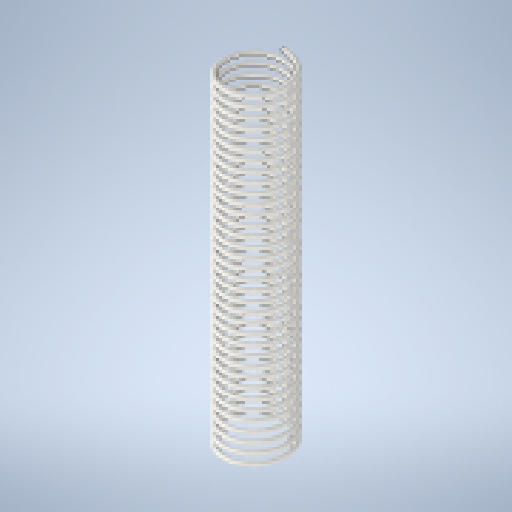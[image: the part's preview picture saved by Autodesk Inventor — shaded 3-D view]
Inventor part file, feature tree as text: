
AUTODESK INVENTOR PART (.ipt)
format: ipt  version: 2025 (Build 290162010, 162A)  size: 1,868,800 bytes
history: native  units: mm
features: sketch x97, plane x32, other x32, sweep x22, extrude x10, helix x4
ambient origin geometry x8: Origin, YZ Plane, XZ Plane, XY Plane, X Axis, Y Axis, Z Axis, Center Point
bodies: Solid1 (feature_tree)
feature tree (197):
  sketch  "3D Sketch2"
  plane  "ArbeitsebeneSweeping1"
  sweep  "Sweep1"
  other  "Erste Umdrehung mit Ösentyp 0(Rechts)"
  sketch  "Sketch8"  dims[d5=0.0mm d6=90.0deg d7=90.0deg d8=0.0mm d9=0.0mm d12=0.2mm]
  plane  "ArbeitsebeneExtrusion7"
  sketch  "Sketch10"  dims[d17=90.0deg d24=0.0mm d25=0.39411mm]
  plane  "ArbeitsebeneSweeping2"
  sweep  "Sweep2"
  other  "Zweite Umdrehung mit Ösentyp 0(Rechts)"
  sketch  "Sketch12"  dims[d26=10.0mm d27=347.619048mm]
  plane  "ArbeitsebeneExtrusion8"
  sketch  "Sketch110"  dims[d396=50.0mm]
  sketch  "3D Sketch20"
  plane  "ArbeitsebeneSweeping3"
  sweep  "Sweep3"
  sketch  "3D Sketch3"
  plane  "ArbeitsebeneSweeping6"
  sweep  "Sweep6"
  other  "Erste Umdrehung mit Ösentyp 0(Links)"
  sketch  "Sketch24"  dims[d171=0.0mm d172=90.0deg]
  plane  "ArbeitsebeneExtrusion5"
  sketch  "Sketch18"  dims[d86=90.0deg d87=20.0mm d90=20.0mm]
  plane  "ArbeitsebeneSweeping7"
  sweep  "Sweep7"
  other  "Zweite Umdrehung mit Ösentyp 0(Links)"
  sketch  "Sketch20"  dims[d149=90.0deg d152=20.0mm]
  plane  "ArbeitsebeneExtrusion6"
  sketch  "Sketch22"  dims[d169=300.0deg d170=1.075mm]
  plane  "ArbeitsebeneSweeping8"
  sweep  "Sweep8"
  other  "Erste Umdrehung mit Ösentyp 1(Links)"
  sketch  "Sketch27"  dims[d175=0.0mm d176=300.0deg]
  plane  "ArbeitsebeneExtrusion9"
  extrude  "Extrusion9"  Depth=10.0mm
  sketch  "Sketch29"  dims[d179=30.0mm d180=90.0deg]
  plane  "ArbeitsebeneSweeping9"
  sweep  "Sweep9"
  other  "Zweite Umdrehung mit Ösentyp 1(Links)"
  sketch  "Sketch32"  dims[d183=0.0mm d184=30.0mm d185=30.0mm d186=30.0mm]
  plane  "ArbeitsebeneExtrusion10"
  sketch  "Sketch34"  dims[d189=1.25mm d190=0.0mm]
  sketch  "3D Sketch22"
  plane  "ArbeitsebeneSweeping10"
  sweep  "Sweep10"
  other  "Erste Umdrehung mit Ösentyp 1(Rechts)"
  sketch  "Sketch42"  dims[d195=40.0mm d196=1.25mm]
  plane  "ArbeitsebeneExtrusion11"
  extrude  "Extrusion11"  Depth=20.0mm
  sketch  "Sketch44"  dims[d199=300.0deg d200=1.075mm]
  plane  "ArbeitsebeneSweeping11"
  sweep  "Sweep11"
  other  "Zweite Umdrehung mit Ösentyp 1(Rechts)"
  sketch  "Sketch112"  dims[d397=29.670597mm]
  plane  "ArbeitsebeneExtrusion12"
  sketch  "Sketch114"  dims[d401=50.0mm]
  sketch  "3D Sketch24"
  plane  "ArbeitsebeneSweeping12"
  sweep  "Sweep12"
  sketch  "Sketch46"  dims[d201=0.0mm d202=90.0deg]
  other  "Erstes Sweeping mit Ösentyp 2(Links)"
  sweep  "SweepingLinksÖse21"
  sketch  "Sketch48"  dims[d206=300.0deg d207=1.075mm]
  other  "Zweites Sweeping mit Ösentyp 2(Links)"
  sweep  "SweepingLinksÖse22"
  sketch  "Sketch50"  dims[d210=1.25mm d211=0.0mm d212=90.0deg d213=300.0deg d214=1.075mm]
  other  "Erstes Sweeping mit Ösentyp 2(Rechts)"
  sweep  "SweepingRechtsÖse21"
  sketch  "Sketch52"  dims[d220=50.0mm]
  other  "Zweites Sweeping mit Ösentyp 2(Rechts)"
  sweep  "SweepingRechtsÖse22"
  other  "Erste Umdrehung mit Ösentyp 3(Links)"
  extrude  "Extrusion1"  TaperAngle=90.0deg  [1 undecoded]
  sweep  "Sweep19"
  other  "Zweite Umdrehung mit Ösentyp 3(Links)"
  extrude  "Extrusion2"  Depth=30.0mm
  sketch  "Sketch60"  dims[d242=90.0deg]
  plane  "ArbeitsebeneSweeping20"
  sweep  "Sweep20"
  other  "Erste Umdrehung mit Ösentyp 3(Rechts)"
  extrude  "Extrusion3"  TaperAngle=0.0deg  [1 undecoded]
  sweep  "Sweep21"
  other  "Zweite Umdrehung mit Ösentyp 3(Rechts)"
  extrude  "Extrusion4"  TaperAngle=90.0deg  [1 undecoded]
  sketch  "Sketch68"  dims[d282=60.0mm]
  plane  "Work Plane46"
  sweep  "Sweep22"
  other  "Erste Umdrehung mit Ösentyp 4(Links)"
  sketch  "Sketch71"  dims[d301=10.0mm d302=15.0mm d303=0.0mm d304=90.0deg d305=90.0deg d306=0.0mm d307=0.0mm]
  plane  "ArbeitsebeneExtrusion13"
  extrude  "Extrusion13"  TaperAngle=90.0deg  [1 undecoded]
  sketch  "Sketch73"  dims[d310=0.7mm]
  plane  "ArbeitsebeneSweeping23"
  sweep  "Sweep23"
  other  "Zweite Umdrehung mit Ösentyp 4(Links)"
  sketch  "Sketch76"  dims[d320=1.125mm]
  plane  "ArbeitsebeneExtrusion14"
  sketch  "Sketch78"  dims[d322=10.0mm d323=15.0mm d324=0.0mm d325=90.0deg d326=90.0deg d327=0.0mm d328=0.0mm d329=70.0mm]
  sketch  "3D Sketch26"
  plane  "ArbeitsebeneSweeping24"
  sweep  "Sweep24"
  other  "Erste Umdrehung mit Ösentyp 4(Rechts)"
  sketch  "Sketch86"  dims[d332=10.0mm d333=15.0mm d334=0.0mm d335=90.0deg d336=90.0deg d337=0.0mm d338=0.0mm d339=70.0mm]
  plane  "Work PlaneExtrusion15"
  extrude  "Extrusion15"  Depth=1.25mm TaperAngle=0.0deg
  sketch  "Sketch88"  dims[d361=10.0mm]
  plane  "ArbeitsebeneSweeping25"
  sweep  "Sweep25"
  other  "Zweite Umdrehung mit Ösentyp 4(Rechts)"
  sketch  "Sketch116"  dims[d404=1.0mm]
  plane  "ArbeitsebeneExtrusion16"
  sketch  "Sketch118"  dims[d406=50.0mm d407=29.670597mm d408=0.0mm d411=60.0mm d423=60.0mm d433=1.0mm d434=0.0mm d435=1.075mm d436=0.7mm d437=10.0mm d438=15.0mm d439=0.0mm d440=90.0deg d441=90.0deg d442=0.0mm d443=0.0mm d444=60.0mm d447=60.0mm d457=1.0mm d458=0.0mm d459=60.0mm d469=90.0deg d478=90.0deg d479=1.075mm d480=0.7mm d481=25.4mm d482=15.0mm d483=0.0mm d484=90.0deg d485=90.0deg d486=0.0mm d487=0.0mm d491=10.0mm d498=10.0mm d501=0.0mm d502=1.0mm d503=0.0mm d504=210.0deg d505=0.0mm d506=0.0mm d507=1.0mm d508=0.0mm d509=29.670597mm d510=0.0mm d511=10.0mm d512=0.0mm d513=1.0mm d514=0.0mm d515=29.670597mm d516=0.0mm d517=0.0mm d518=1.0mm d519=0.0mm d520=1.075mm d521=0.7mm d522=10.0mm d523=15.0mm d524=0.0mm d525=90.0deg d526=90.0deg d527=0.0mm d528=0.0mm d529=60.0mm d530=50.0mm d531=0.0mm d532=1.0mm d533=0.0mm d534=20.0mm d535=210.0deg d536=0.0mm d537=0.0mm d538=1.0mm d539=0.0mm d540=29.670597mm d541=0.0mm d542=50.0mm d543=0.0mm d544=1.0mm d545=0.0mm d546=60.0mm d547=1.075mm d548=0.7mm d549=10.0mm d550=15.0mm d551=0.0mm d552=90.0deg d553=90.0deg d554=0.0mm d555=0.0mm d561=10.0mm d564=0.0mm d565=1.0mm d566=0.0mm d567=10.0mm d569=29.670597mm d570=0.0mm d571=90.0deg d578=0.0mm d579=0.2mm d580=1.0mm d581=0.0mm d584=10.0mm d585=10.0mm d588=29.670597mm d589=0.0mm d590=0.0mm d591=0.0mm d592=0.0mm d593=0.0mm d594=0.0mm d595=0.0mm d596=0.0mm d597=0.0mm d598=0.0mm d599=0.0mm d600=0.0mm d601=0.0mm d602=0.0mm d603=0.0mm d604=0.0mm d605=0.0mm d606=0.0mm d607=0.0mm d608=0.0mm d609=0.0mm d610=0.0mm d611=0.0mm]
  sketch  "3D Sketch28"
  plane  "ArbeitsebeneSweeping26"
  sweep  "Sweep26"
  other  "Erste Umdrehung mit Ösentyp 5(Links)"
  sketch  "Sketch91"  dims[d365=0.0mm]
  plane  "ArbeitsebeneExtrusion17"
  extrude  "Extrusion17"  TaperAngle=0.0deg  [1 undecoded]
  helix  "Coil1"  [1 undecoded]
  other  "Zweite Umdrehung mit Ösentyp 5(Links)"
  sketch  "Sketch95"  dims[d373=20.0mm]
  plane  "ArbeitsebeneExtrusion18"
  helix  "Coil2"  [1 undecoded]
  other  "Erste Umdrehung mit Ösentyp 5(Rechts)"
  sketch  "Sketch99"  dims[d377=210.0deg]
  plane  "ArbeitsebeneExtrusion19"
  helix  "Coil13"  [1 undecoded]
  other  "Zweite Umdrehung mit Ösentyp 5(Rechts)"
  sketch  "Sketch103"  dims[d385=0.0mm]
  plane  "ArbeitsebeneExtrusion20"
  extrude  "Extrusion20"  Depth=40.0mm
  sketch  "Sketch105"  dims[d387=210.0deg]
  helix  "Coil4"  [1 undecoded]
  other  "Erste Spirale mit Ösentyp 6(Links)"
  other  "Zweite Spirale mit Ösentyp 6(Links)"
  other  "Erste Spirale mit Ösentyp 6(Rechts)"
  other  "Zweite Spirale mit Ösentyp 6(Rechts)"
  other  "Srf1"
  sketch  "Sketch4"  dims[d0=0.05mm d1=1.25mm]
  sketch  "Sketch7"  dims[d2=0.39411mm d3=10.0mm d4=347.619048mm]
  other  "Srf2"
  sketch  "Sketch16"  dims[d38=90.0deg d54=10.0mm d55=10.0mm]
  sketch  "Sketch26"  dims[d173=300.0deg d174=1.075mm]
  sketch  "Sketch31"  dims[d181=300.0deg d182=1.125mm]
  sketch  "Sketch36"  dims[d191=300.0deg d192=1.075mm]
  sketch  "Sketch41"  dims[d193=0.0mm d194=90.0deg]
  sketch  "Sketch47"  dims[d203=40.0mm d204=1.25mm d205=0.0mm]
  sketch  "Sketch49"  dims[d208=0.0mm d209=90.0deg]
  sketch  "Sketch51"  dims[d215=0.0mm d216=40.0mm d217=90.0deg]
  sketch  "Sketch53"  dims[d223=90.0deg]
  sketch  "Sketch54"  dims[d226=50.0mm]
  sketch  "Sketch55"  dims[d229=90.0deg]
  sketch  "Sketch56"  dims[d232=50.0mm]
  sketch  "Sketch58"  dims[d235=90.0deg]
  sketch  "Sketch59"  dims[d238=50.0mm]
  sketch  "Sketch61"  dims[d243=60.0mm]
  sketch  "Sketch62"  dims[d255=90.0deg]
  sketch  "Sketch63"  dims[d256=60.0mm]
  sketch  "Sketch64"  dims[d268=90.0deg]
  sketch  "Sketch66"  dims[d269=60.0mm]
  sketch  "Sketch67"  dims[d281=90.0deg]
  sketch  "Sketch69"  dims[d299=1.125mm]
  sketch  "Sketch70"  dims[d300=0.7mm]
  sketch  "Sketch75"  dims[d311=10.0mm d312=15.0mm d313=0.0mm d314=90.0deg d315=90.0deg d316=0.0mm d317=0.0mm d318=70.0mm d319=70.0mm]
  sketch  "Sketch80"  dims[d330=1.125mm]
  sketch  "Sketch85"  dims[d331=0.7mm]
  sketch  "Sketch90"  dims[d364=1.0mm]
  sketch  "Sketch94"  dims[d368=0.0mm]
  sketch  "Sketch98"  dims[d376=20.0mm]
  sketch  "Sketch102"  dims[d384=1.0mm]
  sketch  "Sketch106"  dims[d388=0.0mm]
  sketch  "Sketch107"  dims[d391=50.0mm]
  sketch  "Sketch108"  dims[d394=1.0mm]
  sketch  "Sketch109"  dims[d395=0.0mm]
  sketch  "Sketch13"  dims[d28=0.0mm d29=90.0deg d30=90.0deg d31=0.0mm d32=0.0mm d33=0.2mm]
  sketch  "Sketch33"  dims[d187=90.0deg d188=40.0mm]
  sketch  "Sketch113"  dims[d398=0.0mm]
  sketch  "Sketch77"  dims[d321=0.7mm]
  sketch  "Sketch117"  dims[d405=0.0mm]
  sketch  "Sketch96"  dims[d374=1.0mm]
  sketch  "Sketch97"  dims[d375=0.0mm]
  sketch  "Sketch104"  dims[d386=20.0mm]
  sketch  "Sketch43"  dims[d197=0.0mm d198=90.0deg]
  sketch  "Sketch9"  dims[d13=0.0mm d14=90.0deg]
  sketch  "Sketch87"  dims[d350=10.0mm d352=10.0mm d353=10.0mm d356=10.0mm]
  sketch  "Sketch100"  dims[d378=0.0mm]
  sketch  "Sketch101"  dims[d381=20.0mm]
  sketch  "Sketch28"  dims[d177=1.125mm d178=0.0mm]
  sketch  "Sketch72"  dims[d308=1.125mm]
  sketch  "Sketch92"  dims[d366=10.0mm]
  sketch  "Sketch93"  dims[d367=29.670597mm]
  sketch  "Sketch21"  dims[d155=90.0deg d156=20.0mm]
  sketch  "Sketch15"  dims[d34=0.0mm d36=0.0mm]
  sketch  "Sketch17"  dims[d72=0.0mm d73=0.0mm d79=90.0deg]
  other  "Basisschraube(Rechts)"
  other  "Basisschraube(Links)"
note: 9 required parameter values undecoded (feature->parameter linkage not recoverable at this tier; creation-order binding heuristic only, values carry confidence <= 0.55)
